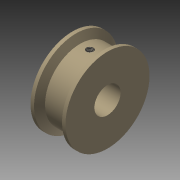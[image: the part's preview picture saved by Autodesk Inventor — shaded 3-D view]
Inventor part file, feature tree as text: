
AUTODESK INVENTOR PART (.ipt)
format: ipt  version: 2015 (Build 190159000, 159)  size: 120,320 bytes
history: native  units: mm
features: sketch x3, extrude x2, revolve x1, plane x1, thread x1
ambient origin geometry x8: Origin, YZ Plane, XZ Plane, XY Plane, X Axis, Y Axis, Z Axis, Center Point
bodies: 实体1 (feature_tree)
feature tree (8):
  revolve  "旋转1"  [1 undecoded]
  extrude  "拉伸1"  Depth=2.0mm
  plane  "工作平面1"
  extrude  "拉伸2"  TaperAngle=120.0deg  [1 undecoded]
  thread  "螺纹1"  [1 undecoded]
  sketch  "草图1"  dims[d1=24.0mm d2=4.0mm]
  sketch  "草图2"  dims[d4=20.0mm d5=2.0mm]
  sketch  "草图3"  dims[d6=120.0deg d7=120.0deg d8=2.0mm d9=90.0deg d10=15.0mm d11=10.0mm d12=0.0mm d13=4.0mm d14=10.0mm d15=0.0mm d16=10.0mm d17=0.0mm]
note: 3 required parameter values undecoded (feature->parameter linkage not recoverable at this tier; creation-order binding heuristic only, values carry confidence <= 0.55)